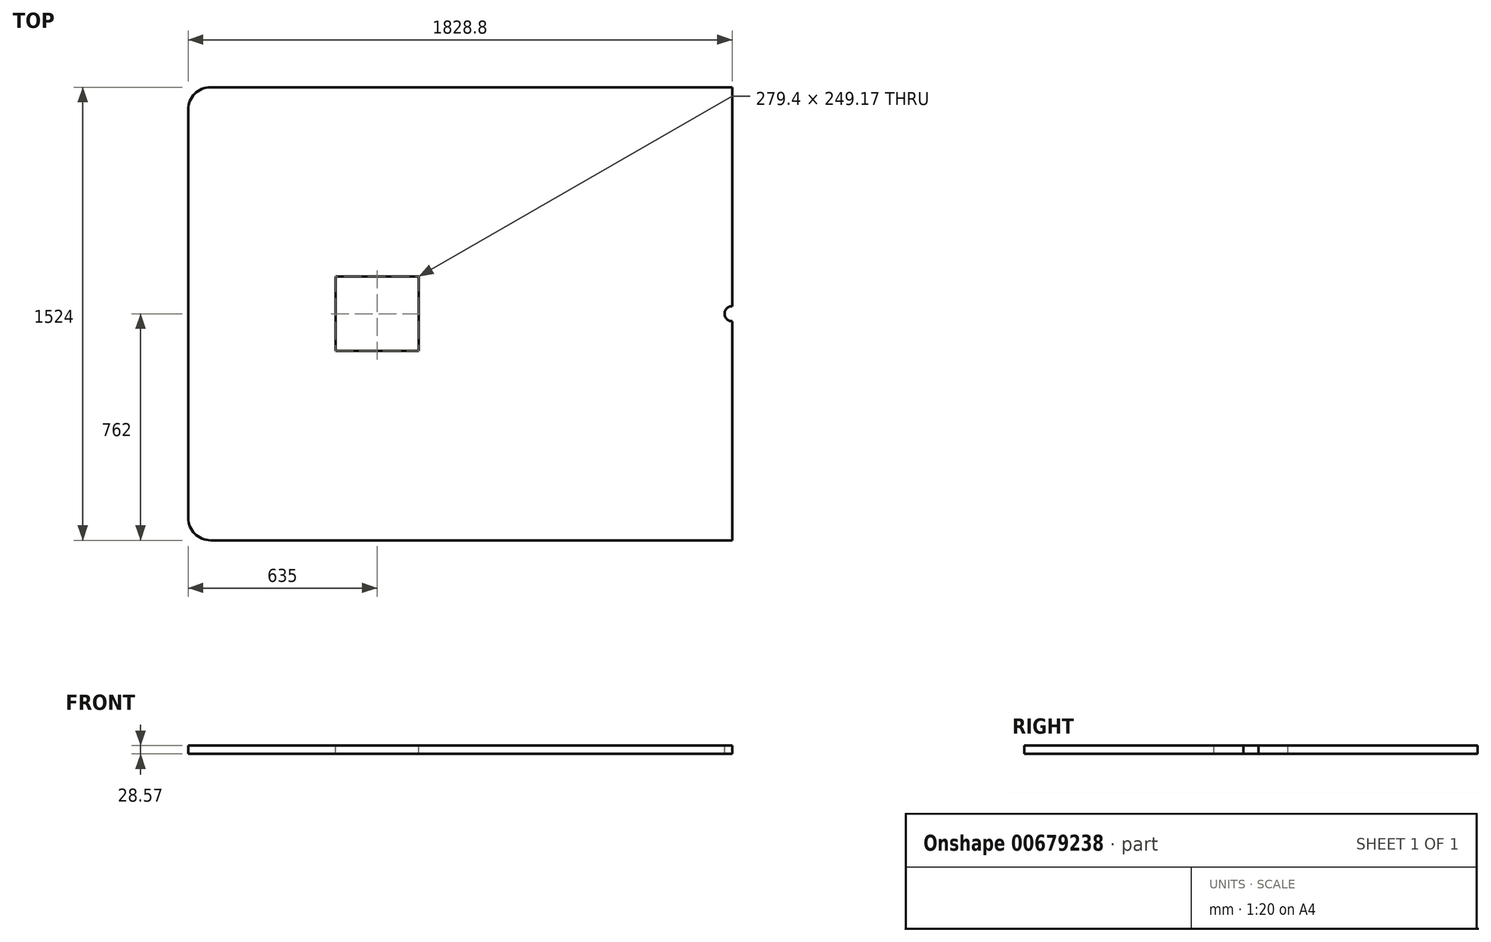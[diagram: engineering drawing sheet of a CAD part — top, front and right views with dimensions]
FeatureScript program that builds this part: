
annotation { "Feature Type Name" : "Feature", "Feature Type Description" : "" }
export const myFeature = defineFeature(function(context is Context, id is Id, definition is map)
    precondition{}
    {
        {
            var Q0;
            Q0=qCreatedBy(makeId("Top.planeOp"),FACE);
            var sketch = newSketch(context, id + "F0", { "sketchPlane" : qUnion([Q0])});
            skLineSegment(sketch, "E0.bottom", {"start": v(914.4, 762) * mm, "end": v(-838.2, 762) * mm});
            skLineSegment(sketch, "E0.top", {"start": v(914.4, -762) * mm, "end": v(-838.2, -762) * mm});
            skLineSegment(sketch, "E0.left", {"start": v(914.4, 762) * mm, "end": v(914.4, -762) * mm});
            skLineSegment(sketch, "E0.right", {"start": v(-914.4, 685.8) * mm, "end": v(-914.4, -685.8) * mm});
            skPoint(sketch, "E0.middle", {"position": v(0, 0) * mm});
            skPoint(sketch, "E1.visualSharp", {"position": v(-914.4, -762) * mm});
            skArc(sketch, "E1.filletArc", {"start": v(-914.4, -685.8) * mm, "mid": v(-892.08, -739.68) * mm, "end": v(-838.2, -762) * mm});
            skPoint(sketch, "E2.visualSharp", {"position": v(-914.4, 762) * mm});
            skArc(sketch, "E2.filletArc", {"start": v(-838.2, 762) * mm, "mid": v(-892.08, 739.68) * mm, "end": v(-914.4, 685.8) * mm});
            skSolve(sketch);
        }
        {
            var Q0;
            Q0=makeQuery(id+"F0.imprint","IMPRINT",FACE,{"disambiguationData":[TD([[makeQuery(id+"F0.imprint","IMPRINT",EDGE,{"derivedFrom":sQuery(id+"F0.wireOp",EDGE,"E0.bottom")}),1.0]])]});
            extrude(context, id + "F1", {"entities" : qUnion([Q0]), "depth" : 28.57 * mm, "offsetDistance" : 25.4 * mm});
        }
        {
            var Q0;
            Q0=makeQuery(id+"F1.opExtrude","CAP_FACE",FACE,{"disambiguationData":[OSD([sQuery(id+"F0.wireOp",EDGE,"E0.bottom"),sQuery(id+"F0.wireOp",EDGE,"E0.top"),sQuery(id+"F0.wireOp",EDGE,"E0.left"),sQuery(id+"F0.wireOp",EDGE,"E0.right"),sQuery(id+"F0.wireOp",EDGE,"E1.filletArc"),sQuery(id+"F0.wireOp",EDGE,"E2.filletArc")])],"isStart":false});
            var sketch = newSketch(context, id + "F2", { "sketchPlane" : qUnion([Q0])});
            skLineSegment(sketch, "E3", {"start": v(-139.7, 0) * mm, "end": v(-279.4, 0) * mm});
            skLineSegment(sketch, "E4.bottom", {"start": v(-139.7, 124.59) * mm, "end": v(-419.1, 124.59) * mm});
            skLineSegment(sketch, "E4.top", {"start": v(-139.7, -124.59) * mm, "end": v(-419.1, -124.59) * mm});
            skLineSegment(sketch, "E4.left", {"start": v(-139.7, 124.59) * mm, "end": v(-139.7, -124.59) * mm});
            skLineSegment(sketch, "E4.right", {"start": v(-419.1, 124.59) * mm, "end": v(-419.1, -124.59) * mm});
            skPoint(sketch, "E4.middle", {"position": v(-279.4, 0) * mm});
            skCircle(sketch, "E5", {"center": v(914.4, 0) * mm, "radius": 25.4 * mm});
            skSolve(sketch);
        }
        {
            var Q0;
            {var subQ3=sQuery(id+"F2.wireOp",EDGE,"E4.bottom");Q0=makeQuery(id+"F2.imprint","IMPRINT",FACE,{"disambiguationData":[TD([[makeQuery(id+"F2.imprint","IMPRINT",EDGE,{"derivedFrom":subQ3}),1.0]])]});}
            var Q1;
            {var subQ0=sQuery(id+"F2.wireOp",EDGE,"E5");var subQ1=makeQuery(id+"F1.opExtrude","CAP_EDGE",EDGE,{"disambiguationData":[OSD([sQuery(id+"F0.wireOp",EDGE,"E0.left")])],"isStart":false});var subQ2=makeQuery(id+"F2.imprint","INTERSECT",VERTEX,{"disambiguationData":[OD(0.0)],"derivedFrom":[subQ1,subQ0]});Q1=makeQuery(id+"F2.imprint","IMPRINT",FACE,{"disambiguationData":[TD([[makeQuery(id+"F2.imprint","IMPRINT",EDGE,{"disambiguationData":[TD([[subQ2,-1.0]])],"derivedFrom":subQ0}),1.0]])]});}
            extrude(context, id + "F3", {"entities" : qUnion([Q0, Q1]), "operationType" : NewBodyOperationType.REMOVE, "oppositeDirection" : true, "depth" : 28.57 * mm, "offsetDistance" : 25.4 * mm});
        }
    });
